# Revit family: Showerhead-Water-Saving-American_Standard-Colony Pro-1660512_Series
name_source: partatom
category: Plumbing Fixtures
units: mm (PartAtom-declared; Revit-internal decimal feet)

## family parameters
Always vertical = No
Cut with Voids When Loaded = No
OmniClass Number = 23.45.05.14.17
OmniClass Title = Showers
Part Type = Normal
Room Calculation Point = No
Round Connector Dimension = Use Diameter
Shared = Yes
Work Plane-Based = Yes

## types (2) — shared parameters
1660240 Standard Shower Arm and Flange = No
1660241 Modern Shower Arm and Flange = No
Assembly Code = D2010700
CEC Compliant = Yes
CW Connection = Yes
CWFU = 3
CalGreen Compliant = Yes
Default Elevation = 0"
Description = Colony® Pro 1.75 gpm/6.6 L/min Water-Saving Showerhead
Flow Rate = 1.75 gpm (6.6 L/min)
HW Connection = Yes
HWFU = 3
Height = 3 5/16"
Installation Type = Shower Arm Mounted
Length = 3 11/16"
Manufacturer = American Standard
NPT Connection Size = 1/2"
Product Documentation Link = https://lixil.cdn.celum.cloud
Product Page URL = https://www.americanstandard-us.com
URL = https://www.americanstandard-us.com
Vent Connection = No
WFU = 4
Waste Connection = Yes

## per-type parameters (varying)
| type | Finish | Material |
| 1660512.002 | Metal-American Standard-002-Polished Chrome | Metal-American Standard-002-Polished Chrome |
| 1660512.295 | Metal-American Standard-295-Brushed Nickel | Metal-American Standard-295-Brushed Nickel |

note: column(s) folded — value = type name in every type: Model

## geometry (parser evidence)
native form markers: Sweep x2
no freeform markers — native parametric forms only
